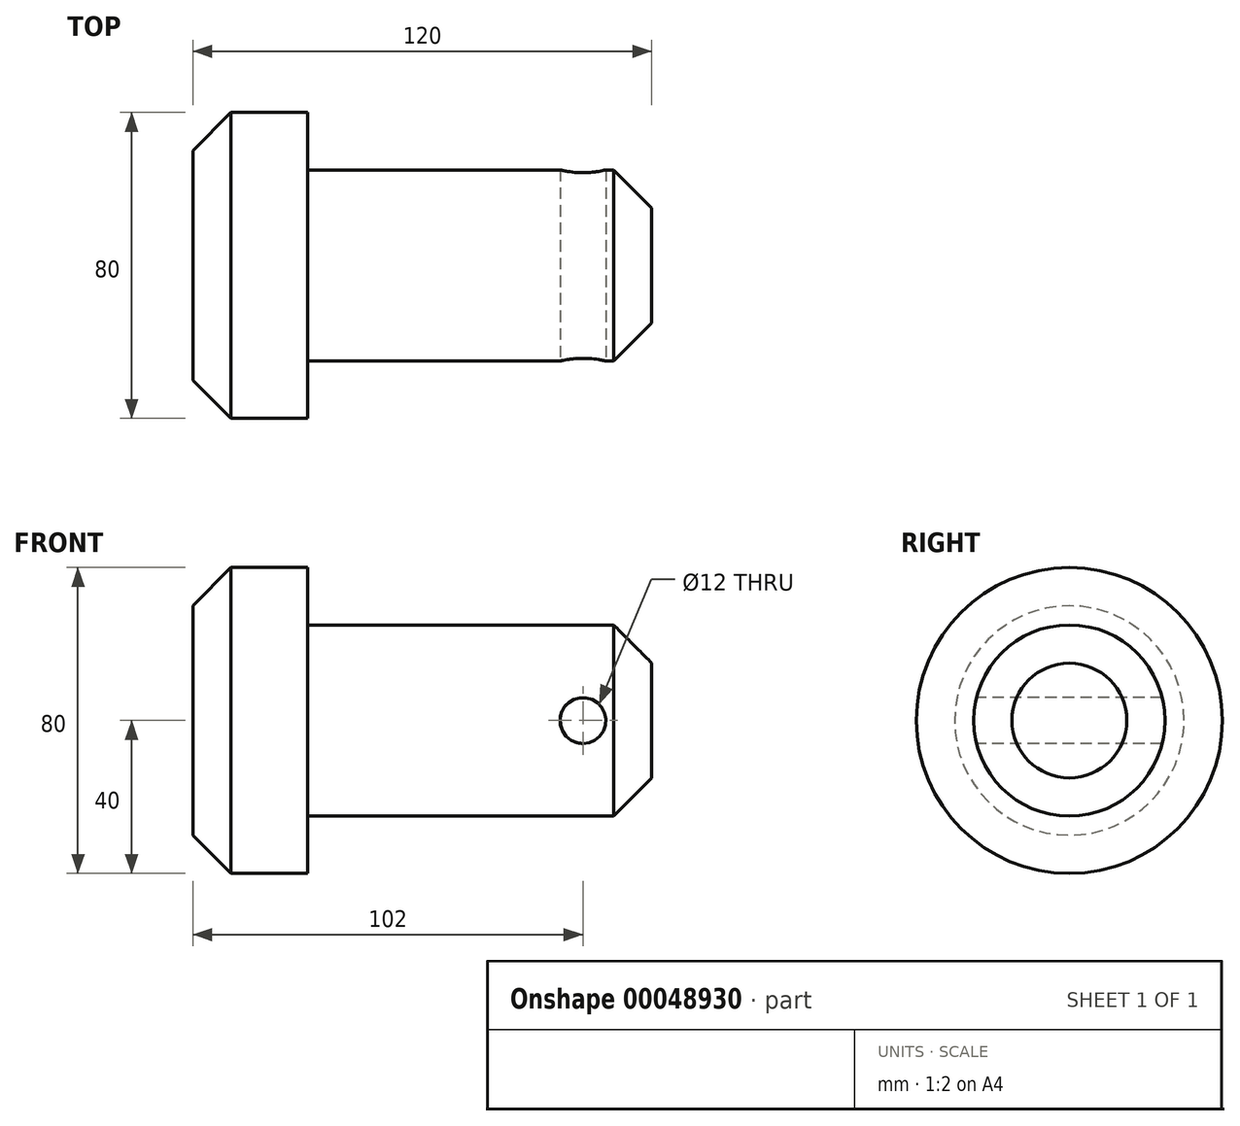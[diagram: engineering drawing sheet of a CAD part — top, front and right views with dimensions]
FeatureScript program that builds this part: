
annotation { "Feature Type Name" : "Feature", "Feature Type Description" : "" }
export const myFeature = defineFeature(function(context is Context, id is Id, definition is map)
    precondition{}
    {
        {
            var Q0;
            Q0=qCreatedBy(makeId("Front.planeOp"),FACE);
            var sketch = newSketch(context, id + "F0", { "sketchPlane" : qUnion([Q0])});
            skLineSegment(sketch, "E0", {"start": v(0, 0) * mm, "end": v(0, 25) * mm});
            skLineSegment(sketch, "E1", {"start": v(0, 25) * mm, "end": v(-90, 25) * mm});
            skLineSegment(sketch, "E2", {"start": v(-90, 25) * mm, "end": v(-90, 40) * mm});
            skLineSegment(sketch, "E3", {"start": v(-90, 40) * mm, "end": v(-120, 40) * mm});
            skLineSegment(sketch, "E4", {"start": v(-120, 40) * mm, "end": v(-120, 0) * mm});
            skLineSegment(sketch, "E5", {"start": v(-120, 0) * mm, "end": v(0, 0) * mm});
            skSolve(sketch);
        }
        {
            var Q0;
            Q0=makeQuery(id+"F0.imprint","IMPRINT",FACE,{"disambiguationData":[TD([[makeQuery(id+"F0.imprint","IMPRINT",EDGE,{"derivedFrom":sQuery(id+"F0.wireOp",EDGE,"E0")}),1.0]])]});
            var Q1;
            Q1=sQuery(id+"F0.wireOp",EDGE,"E5");
            revolve(context, id + "F1", {"entities" : qUnion([Q0]), "axis" : qUnion([Q1]), "revolveType" : RevolveType.FULL});
        }
        {
            var Q0;
            Q0=makeQuery(id+"F1.opRevolve","SWEPT_EDGE",EDGE,{"disambiguationData":[OSD([sQuery(id+"F0.wireOp",EDGE,"E3"),sQuery(id+"F0.wireOp",EDGE,"E4")])]});
            var Q1;
            Q1=makeQuery(id+"F1.opRevolve","SWEPT_EDGE",EDGE,{"disambiguationData":[OSD([sQuery(id+"F0.wireOp",EDGE,"E0"),sQuery(id+"F0.wireOp",EDGE,"E1")])]});
            chamfer(context, id + "F2", {"entities" : qUnion([Q0, Q1]), "chamferType" : ChamferType.OFFSET_ANGLE, "width" : 10 * mm, "oppositeDirection" : false, "angle" : 45 * degree, "tangentPropagation" : true});
        }
        {
            var Q0;
            Q0=qCreatedBy(makeId("Front.planeOp"),FACE);
            var sketch = newSketch(context, id + "F3", { "sketchPlane" : qUnion([Q0])});
            skLineSegment(sketch, "E6", {"start": v(0, 0) * mm, "end": v(-18, 0) * mm, "construction": true});
            skCircle(sketch, "E7", {"center": v(-18, 0) * mm, "radius": 6 * mm});
            skSolve(sketch);
        }
        {
            var Q0;
            Q0 = qSketchRegion(id + "F3", true);
            var Q1;
            Q1=sQuery(id+"F3.wireOp",EDGE,"E7");
            extrude(context, id + "F4", {"entities" : qUnion([Q0]), "operationType" : NewBodyOperationType.REMOVE, "surfaceEntities" : qUnion([Q1]), "endBound" : BoundingType.THROUGH_ALL, "oppositeDirection" : true, "depth" : 25 * mm, "hasSecondDirection" : true, "secondDirectionBound" : SecondDirectionBoundingType.THROUGH_ALL, "secondDirectionOppositeDirection" : false, "secondDirectionDepth" : 25 * mm});
        }
    });
